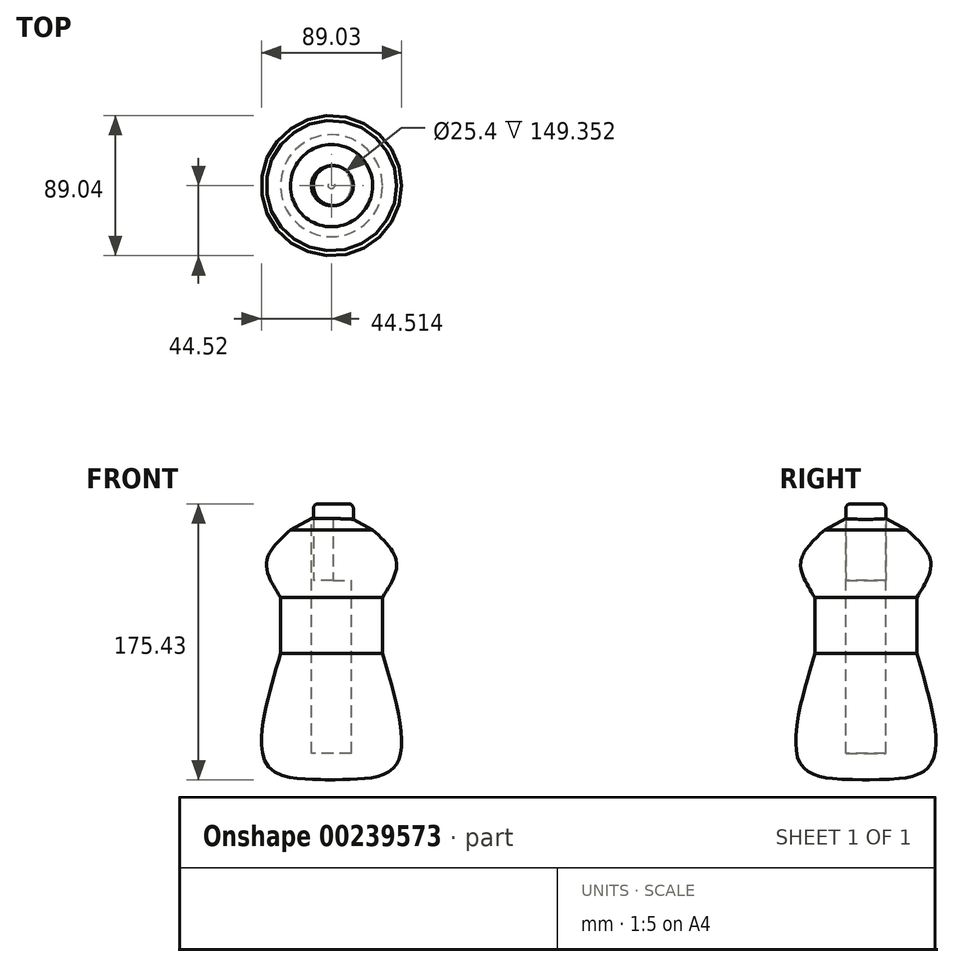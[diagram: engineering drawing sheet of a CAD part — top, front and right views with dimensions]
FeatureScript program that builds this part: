
annotation { "Feature Type Name" : "Feature", "Feature Type Description" : "" }
export const myFeature = defineFeature(function(context is Context, id is Id, definition is map)
    precondition{}
    {
        {
            var Q0;
            Q0=qCreatedBy(makeId("Front.planeOp"),FACE);
            var sketch = newSketch(context, id + "F0", { "sketchPlane" : qUnion([Q0])});
            skLineSegment(sketch, "E0", {"start": v(2, 44.57) * mm, "end": v(-10.7, 44.57) * mm});
            skLineSegment(sketch, "E1", {"start": v(-10.7, 44.57) * mm, "end": v(-10.7, 39.49) * mm});
            skLineSegment(sketch, "E2", {"start": v(-10.7, 39.49) * mm, "end": v(-24.1, 32.23) * mm});
            skFitSpline(sketch, "E3", {"points": [v(-24.1, 32.23) * mm, v(-39.3, 11.8) * mm, v(-30.4, -10.78) * mm], "startDerivative": vector(-42.4, -39.14) * mm, "endDerivative": vector(29.88, -48.91) * mm});
            skLineSegment(sketch, "E4", {"start": v(-30.4, -10.78) * mm, "end": v(-30.4, -46.34) * mm});
            skFitSpline(sketch, "E5", {"points": [v(-30.4, -46.34) * mm, v(-38.9, -117.28) * mm, v(0, -126.52) * mm], "startDerivative": vector(-44.95, -151.51) * mm, "endDerivative": vector(113.14, -1.83) * mm});
            skFitSpline(sketch, "E6", {"points": [v(29.35, -46.34) * mm, v(35.75, -109.59) * mm, v(0, -126.52) * mm], "startDerivative": vector(58.13, -161.15) * mm, "endDerivative": vector(-125.08, 8.43) * mm});
            skLineSegment(sketch, "E7", {"start": v(2, 44.57) * mm, "end": v(2, -126.62) * mm});
            skPoint(sketch, "E8.start.orphan", {"position": v(14.7, 54.16) * mm});
            skPoint(sketch, "E9.start.orphan", {"position": v(14.7, 44.57) * mm});
            skPoint(sketch, "E10.end.orphan", {"position": v(2, 54.16) * mm});
            skPoint(sketch, "E11.start.orphan", {"position": v(-10.7, 54.16) * mm});
            skLineSegment(sketch, "E12", {"start": v(-10.7, 44.57) * mm, "end": v(-10.7, 49.65) * mm});
            skLineSegment(sketch, "E13", {"start": v(-10.7, 49.65) * mm, "end": v(2, 49.65) * mm});
            skLineSegment(sketch, "E14", {"start": v(2, 49.65) * mm, "end": v(2, 44.57) * mm});
            skSolve(sketch);
        }
        {
            var Q0;
            Q0 = qSketchRegion(id + "F0", true);
            var Q1;
            Q1=sQuery(id+"F0.wireOp",EDGE,"E7");
            revolve(context, id + "F1", {"entities" : qUnion([Q0]), "axis" : qUnion([Q1]), "revolveType" : RevolveType.FULL});
        }
        {
            var Q0;
            Q0=makeQuery(id+"F1.opRevolve","SWEPT_FACE",FACE,{"disambiguationData":[OSD([sQuery(id+"F0.wireOp",EDGE,"E13")])]});
            extrude(context, id + "F2", {"entities" : qUnion([Q0]), "operationType" : NewBodyOperationType.REMOVE, "endBound" : BoundingType.SYMMETRIC, "oppositeDirection" : true, "depth" : 319.02 * mm});
        }
        {
            var Q0;
            Q0=qCreatedBy(makeId("Top.planeOp"),FACE);
            var sketch = newSketch(context, id + "F3", { "sketchPlane" : qUnion([Q0])});
            skCircle(sketch, "E15", {"center": v(3.15, 0) * mm, "radius": 12.67 * mm});
            skSolve(sketch);
        }
        {
            var Q0;
            Q0 = qSketchRegion(id + "F3", true);
            extrude(context, id + "F4", {"entities" : qUnion([Q0]), "operationType" : NewBodyOperationType.ADD, "depth" : 48.77 * mm});
        }
        {
            var Q0;
            Q0=makeQuery(id+"F4.opExtrude","CAP_EDGE",EDGE,{"disambiguationData":[OSD([sQuery(id+"F3.wireOp",EDGE,"E15")])],"isStart":false});
            fillet(context, id + "F5", {"entities" : qUnion([Q0]), "radius" : 3.07 * mm, "tangentPropagation" : true, "allowEdgeOverflow" : false});
        }
    });
